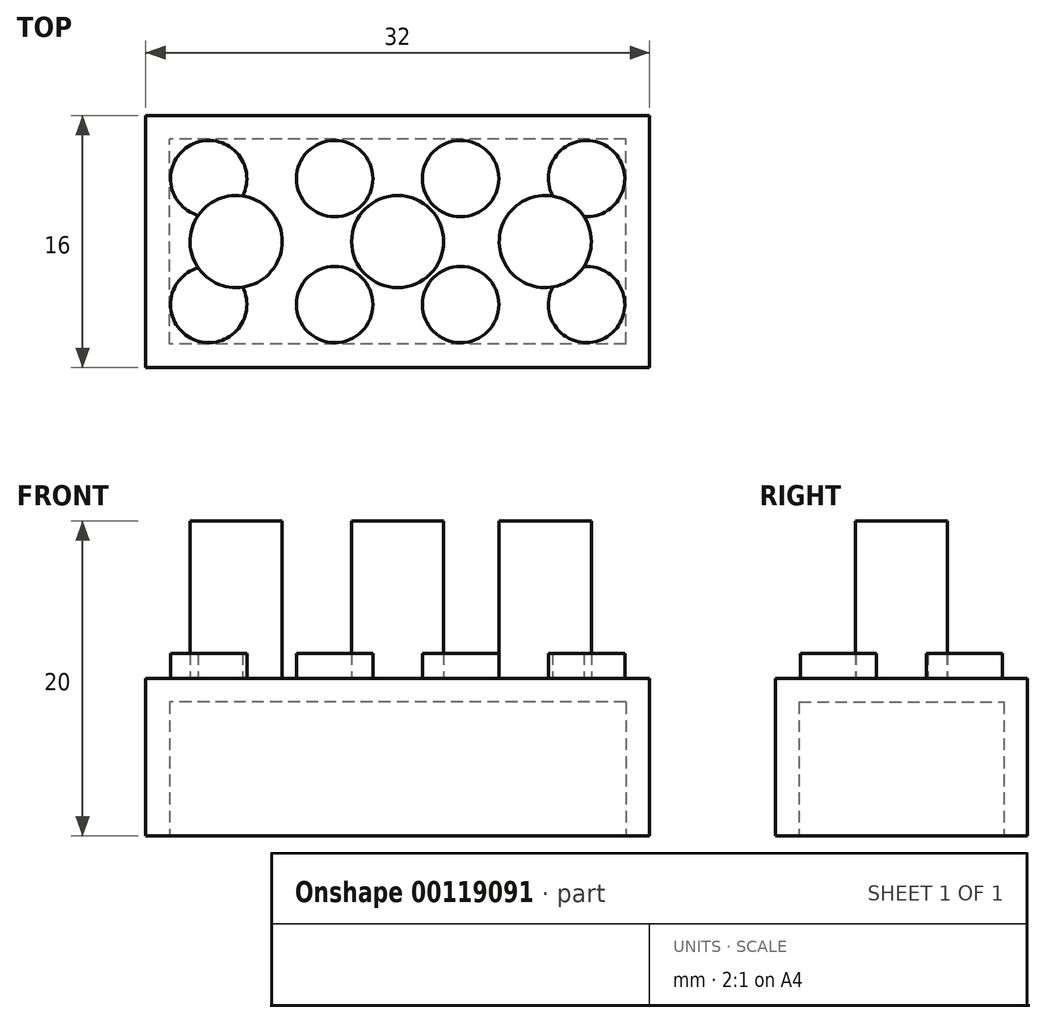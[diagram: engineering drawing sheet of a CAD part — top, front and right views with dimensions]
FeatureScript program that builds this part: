
annotation { "Feature Type Name" : "Feature", "Feature Type Description" : "" }
export const myFeature = defineFeature(function(context is Context, id is Id, definition is map)
    precondition{}
    {
        {
            var Q0;
            Q0=qCreatedBy(makeId("Top.planeOp"),FACE);
            var sketch = newSketch(context, id + "F0", { "sketchPlane" : qUnion([Q0])});
            skLineSegment(sketch, "E0.bottom", {"start": v(16, -8) * mm, "end": v(-16, -8) * mm});
            skLineSegment(sketch, "E0.top", {"start": v(16, 8) * mm, "end": v(-16, 8) * mm});
            skLineSegment(sketch, "E0.left", {"start": v(16, -8) * mm, "end": v(16, 8) * mm});
            skLineSegment(sketch, "E0.right", {"start": v(-16, -8) * mm, "end": v(-16, 8) * mm});
            skPoint(sketch, "E0.middle", {"position": v(0, 0) * mm});
            skSolve(sketch);
        }
        {
            var Q0;
            Q0 = qSketchRegion(id + "F0", true);
            extrude(context, id + "F1", {"entities" : qUnion([Q0]), "depth" : 10 * mm});
        }
        {
            var Q0;
            Q0=makeQuery(id+"F1.opExtrude","CAP_FACE",FACE,{"disambiguationData":[OSD([sQuery(id+"F0.wireOp",EDGE,"E0.bottom"),sQuery(id+"F0.wireOp",EDGE,"E0.top"),sQuery(id+"F0.wireOp",EDGE,"E0.left"),sQuery(id+"F0.wireOp",EDGE,"E0.right")])],"isStart":true});
            shell(context, id + "F2", {"entities" : qUnion([Q0]), "thickness" : 1.5 * mm});
        }
        {
            var Q0;
            Q0=makeQuery(id+"F1.opExtrude","CAP_FACE",FACE,{"disambiguationData":[OSD([sQuery(id+"F0.wireOp",EDGE,"E0.bottom"),sQuery(id+"F0.wireOp",EDGE,"E0.top"),sQuery(id+"F0.wireOp",EDGE,"E0.left"),sQuery(id+"F0.wireOp",EDGE,"E0.right")])],"isStart":false});
            var sketch = newSketch(context, id + "F3", { "sketchPlane" : qUnion([Q0])});
            skCircle(sketch, "E1", {"center": v(-12, -4) * mm, "radius": 2.43 * mm});
            skCircle(sketch, "E2.0.1.0", {"center": v(-12, 4) * mm, "radius": 2.43 * mm});
            skCircle(sketch, "E2.1.0.0", {"center": v(-4, -4) * mm, "radius": 2.43 * mm});
            skCircle(sketch, "E2.1.1.0", {"center": v(-4, 4) * mm, "radius": 2.43 * mm});
            skCircle(sketch, "E2.2.0.0", {"center": v(4, -4) * mm, "radius": 2.43 * mm});
            skCircle(sketch, "E2.2.1.0", {"center": v(4, 4) * mm, "radius": 2.43 * mm});
            skCircle(sketch, "E2.3.0.0", {"center": v(12, -4) * mm, "radius": 2.43 * mm});
            skCircle(sketch, "E2.3.1.0", {"center": v(12, 4) * mm, "radius": 2.43 * mm});
            skLineSegment(sketch, "E2.direction1", {"start": v(-12, -4) * mm, "end": v(-4, -4) * mm, "construction": true});
            skLineSegment(sketch, "E2.direction2", {"start": v(-12, -4) * mm, "end": v(-12, 4) * mm, "construction": true});
            skSolve(sketch);
        }
        {
            var Q0;
            Q0 = qSketchRegion(id + "F3", true);
            extrude(context, id + "F4", {"entities" : qUnion([Q0]), "operationType" : NewBodyOperationType.ADD, "depth" : 1.6 * mm});
        }
        {
            var Q0;
            Q0=makeQuery(id+"F1.opExtrude","CAP_FACE",FACE,{"disambiguationData":[OSD([sQuery(id+"F0.wireOp",EDGE,"E0.bottom"),sQuery(id+"F0.wireOp",EDGE,"E0.top"),sQuery(id+"F0.wireOp",EDGE,"E0.left"),sQuery(id+"F0.wireOp",EDGE,"E0.right")])],"isStart":false});
            var sketch = newSketch(context, id + "F5", { "sketchPlane" : qUnion([Q0])});
            skCircle(sketch, "E3", {"center": v(-10.26, 0) * mm, "radius": 2.93 * mm});
            skCircle(sketch, "E4", {"center": v(0, 0) * mm, "radius": 2.93 * mm});
            skCircle(sketch, "E5", {"center": v(9.38, 0) * mm, "radius": 2.93 * mm});
            skLineSegment(sketch, "E6", {"start": v(-10.26, 0) * mm, "end": v(0, 0) * mm});
            skLineSegment(sketch, "E7", {"start": v(0, 0) * mm, "end": v(9.38, 0) * mm});
            skSolve(sketch);
        }
        {
            var Q0;
            Q0 = qSketchRegion(id + "F5", true);
            extrude(context, id + "F6", {"entities" : qUnion([Q0]), "operationType" : NewBodyOperationType.ADD, "depth" : 10 * mm});
        }
    });
